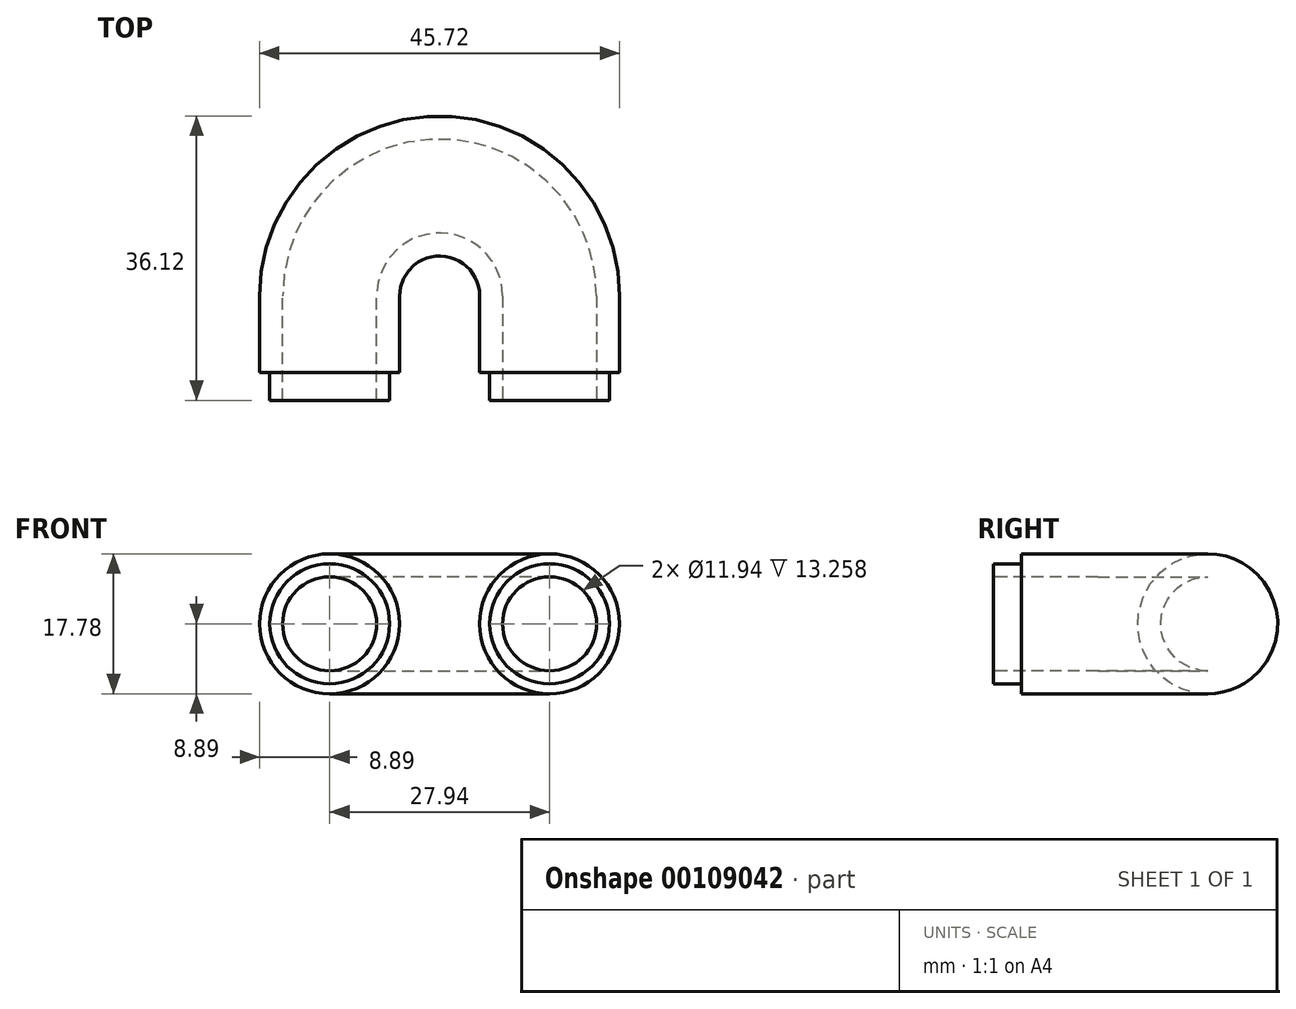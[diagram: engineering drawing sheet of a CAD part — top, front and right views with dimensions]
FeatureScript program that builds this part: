
annotation { "Feature Type Name" : "Feature", "Feature Type Description" : "" }
export const myFeature = defineFeature(function(context is Context, id is Id, definition is map)
    precondition{}
    {
        {
            var Q0;
            Q0=qCreatedBy(makeId("Top.planeOp"),FACE);
            var sketch = newSketch(context, id + "F0", { "sketchPlane" : qUnion([Q0])});
            skLineSegment(sketch, "E0", {"start": v(0, 0) * mm, "end": v(0, 9.7) * mm});
            skArc(sketch, "E1", {"start": v(0, 9.7) * mm, "mid": v(13.97, 23.67) * mm, "end": v(27.94, 9.7) * mm});
            skLineSegment(sketch, "E2", {"start": v(27.94, 9.7) * mm, "end": v(27.94, 0) * mm});
            skLineSegment(sketch, "E3", {"start": v(0, 0) * mm, "end": v(0, -5.08) * mm});
            skLineSegment(sketch, "E4", {"start": v(27.94, 0) * mm, "end": v(27.94, -3.56) * mm});
            skSolve(sketch);
        }
        {
            var Q0;
            Q0=qCreatedBy(makeId("Front.planeOp"),FACE);
            var sketch = newSketch(context, id + "F1", { "sketchPlane" : qUnion([Q0])});
            skCircle(sketch, "E5", {"center": v(0, 0) * mm, "radius": 8.9 * mm});
            skCircle(sketch, "E6", {"center": v(0, 0) * mm, "radius": 5.97 * mm});
            skSolve(sketch);
        }
        {
            var Q0;
            Q0=makeQuery(id+"F1.imprint","IMPRINT",FACE,{"disambiguationData":[TD([[makeQuery(id+"F1.imprint","IMPRINT",EDGE,{"derivedFrom":sQuery(id+"F1.wireOp",EDGE,"E5")}),1.0]])]});
            var Q1;
            Q1=sQuery(id+"F0.wireOp",EDGE,"E0");
            var Q2;
            Q2=sQuery(id+"F0.wireOp",EDGE,"E1");
            var Q3;
            Q3=sQuery(id+"F0.wireOp",EDGE,"E2");
            var Q4;
            Q4=sQuery(id+"F0.wireOp",EDGE,"E4");
            sweep(context, id + "F2", {"profiles" : qUnion([Q0]), "path" : qUnion([Q1, Q2, Q3, Q4])});
        }
        {
            var Q0;
            Q0=makeQuery(id+"F2.opSweep","CAP_FACE",FACE,{"disambiguationData":[OSD([sQuery(id+"F0.wireOp",VERTEX,"E0.start"),sQuery(id+"F1.wireOp",EDGE,"E5"),sQuery(id+"F1.wireOp",EDGE,"E6")])],"isStart":true});
            extrude(context, id + "F3", {"entities" : qUnion([Q0]), "operationType" : NewBodyOperationType.ADD, "depth" : 3.56 * mm});
        }
        {
            var Q0;
            Q0=makeQuery(id+"F3.opExtrude","CAP_FACE",FACE,{"disambiguationData":[OSD([sQuery(id+"F0.wireOp",VERTEX,"E0.start"),sQuery(id+"F1.wireOp",EDGE,"E5"),sQuery(id+"F1.wireOp",EDGE,"E6")])],"isStart":false});
            var sketch = newSketch(context, id + "F4", { "sketchPlane" : qUnion([Q0])});
            skCircle(sketch, "E7", {"center": v(0, 0) * mm, "radius": 7.62 * mm});
            skSolve(sketch);
        }
        {
            var Q0;
            Q0=makeQuery(id+"F2.opSweep","CAP_FACE",FACE,{"disambiguationData":[OSD([sQuery(id+"F0.wireOp",VERTEX,"E4.end"),sQuery(id+"F1.wireOp",EDGE,"E5"),sQuery(id+"F1.wireOp",EDGE,"E6")])],"isStart":false});
            var sketch = newSketch(context, id + "F5", { "sketchPlane" : qUnion([Q0])});
            skCircle(sketch, "E8", {"center": v(27.94, 0) * mm, "radius": 7.62 * mm});
            skSolve(sketch);
        }
        {
            var Q0;
            Q0=makeQuery(id+"F4.imprint","IMPRINT",FACE,{"disambiguationData":[TD([[makeQuery(id+"F4.imprint","IMPRINT",EDGE,{"derivedFrom":sQuery(id+"F4.wireOp",EDGE,"E7")}),-1.0]])]});
            extrude(context, id + "F6", {"entities" : qUnion([Q0]), "operationType" : NewBodyOperationType.REMOVE, "oppositeDirection" : true, "depth" : 3.56 * mm});
        }
        {
            var Q0;
            Q0=makeQuery(id+"F5.imprint","IMPRINT",FACE,{"disambiguationData":[TD([[makeQuery(id+"F5.imprint","IMPRINT",EDGE,{"derivedFrom":sQuery(id+"F5.wireOp",EDGE,"E8")}),-1.0]])]});
            extrude(context, id + "F7", {"entities" : qUnion([Q0]), "operationType" : NewBodyOperationType.REMOVE, "oppositeDirection" : true, "depth" : 3.56 * mm});
        }
    });
